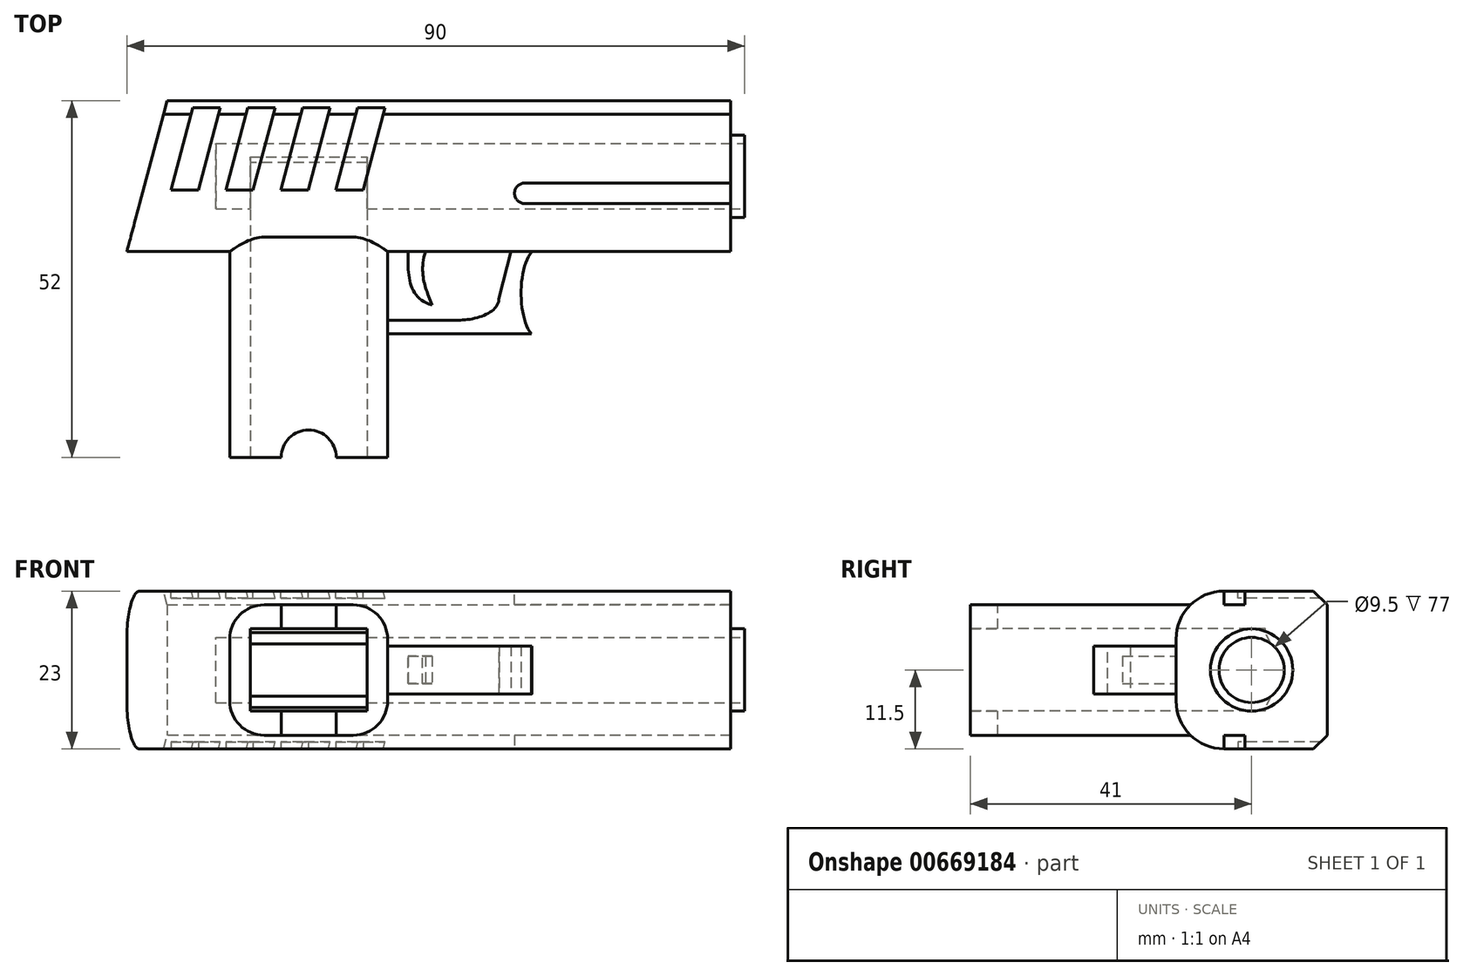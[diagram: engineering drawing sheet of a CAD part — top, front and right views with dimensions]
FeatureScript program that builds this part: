
annotation { "Feature Type Name" : "Feature", "Feature Type Description" : "" }
export const myFeature = defineFeature(function(context is Context, id is Id, definition is map)
    precondition{}
    {
        {
            var Q0;
            Q0=qCreatedBy(makeId("Top.planeOp"),FACE);
            var sketch = newSketch(context, id + "F0", { "sketchPlane" : qUnion([Q0])});
            skLineSegment(sketch, "E0", {"start": v(49.59, 22) * mm, "end": v(49.59, 0) * mm});
            skLineSegment(sketch, "E1", {"start": v(49.59, 0) * mm, "end": v(-0.41, 0) * mm});
            skLineSegment(sketch, "E2", {"start": v(-0.41, 0) * mm, "end": v(-0.41, -30) * mm});
            skLineSegment(sketch, "E3", {"start": v(-0.41, -30) * mm, "end": v(-23.41, -30) * mm});
            skLineSegment(sketch, "E4", {"start": v(-23.41, -30) * mm, "end": v(-23.41, 0) * mm});
            skLineSegment(sketch, "E5", {"start": v(-23.41, 0) * mm, "end": v(-38.41, 0) * mm});
            skLineSegment(sketch, "E6", {"start": v(-32.52, 22) * mm, "end": v(49.59, 22) * mm});
            skLineSegment(sketch, "E7", {"start": v(-38.41, 0) * mm, "end": v(-32.52, 22) * mm});
            skSolve(sketch);
        }
        {
            var Q0;
            Q0=makeQuery(id+"F0.imprint","IMPRINT",FACE,{"disambiguationData":[TD([[makeQuery(id+"F0.imprint","IMPRINT",EDGE,{"derivedFrom":sQuery(id+"F0.wireOp",EDGE,"E0")}),-1.0]])]});
            extrude(context, id + "F1", {"entities" : qUnion([Q0]), "endBound" : BoundingType.SYMMETRIC, "depth" : 19 * mm, "offsetDistance" : 25 * mm});
        }
        {
            var Q0;
            Q0=makeQuery(id+"F1.opExtrude","CAP_FACE",FACE,{"disambiguationData":[OSD([sQuery(id+"F0.wireOp",EDGE,"E0"),sQuery(id+"F0.wireOp",EDGE,"E1"),sQuery(id+"F0.wireOp",EDGE,"E2"),sQuery(id+"F0.wireOp",EDGE,"E3"),sQuery(id+"F0.wireOp",EDGE,"E4"),sQuery(id+"F0.wireOp",EDGE,"E5"),sQuery(id+"F0.wireOp",EDGE,"NrAtbqXy-u60X-30Q2-Hl1u-7mO5fDowlZYq"),sQuery(id+"F0.wireOp",EDGE,"E6")])],"isStart":false});
            var sketch = newSketch(context, id + "F2", { "sketchPlane" : qUnion([Q0])});
            skLineSegment(sketch, "E8", {"start": v(-32.52, 22) * mm, "end": v(49.59, 22) * mm});
            skLineSegment(sketch, "E9", {"start": v(49.59, 22) * mm, "end": v(49.59, 0) * mm});
            skLineSegment(sketch, "E10", {"start": v(49.59, 0) * mm, "end": v(-38.41, 0) * mm});
            skLineSegment(sketch, "E11", {"start": v(-38.41, 0) * mm, "end": v(-32.52, 22) * mm});
            skSolve(sketch);
        }
        {
            var Q0;
            Q0=makeQuery(id+"F2.imprint","IMPRINT",FACE,{"disambiguationData":[TD([[makeQuery(id+"F2.imprint","IMPRINT",EDGE,{"derivedFrom":sQuery(id+"F2.wireOp",EDGE,"E8")}),-1.0]])]});
            extrude(context, id + "F3", {"entities" : qUnion([Q0]), "operationType" : NewBodyOperationType.ADD, "depth" : 2 * mm, "offsetDistance" : 25 * mm});
        }
        {
            var Q0;
            Q0=makeQuery(id+"F1.opExtrude","CAP_FACE",FACE,{"disambiguationData":[OSD([sQuery(id+"F0.wireOp",EDGE,"E0"),sQuery(id+"F0.wireOp",EDGE,"E1"),sQuery(id+"F0.wireOp",EDGE,"E2"),sQuery(id+"F0.wireOp",EDGE,"E3"),sQuery(id+"F0.wireOp",EDGE,"E4"),sQuery(id+"F0.wireOp",EDGE,"E5"),sQuery(id+"F0.wireOp",EDGE,"E6"),sQuery(id+"F0.wireOp",EDGE,"E7")])],"isStart":true});
            var sketch = newSketch(context, id + "F4", { "sketchPlane" : qUnion([Q0])});
            skLineSegment(sketch, "E12", {"start": v(-38.41, 0) * mm, "end": v(49.59, 0) * mm});
            skLineSegment(sketch, "E13", {"start": v(49.59, 0) * mm, "end": v(49.59, -22) * mm});
            skLineSegment(sketch, "E14", {"start": v(49.59, -22) * mm, "end": v(-32.52, -22) * mm});
            skLineSegment(sketch, "E15", {"start": v(-38.41, 0) * mm, "end": v(-32.52, -22) * mm});
            skSolve(sketch);
        }
        {
            var Q0;
            {var subQ0=sQuery(id+"F4.wireOp",EDGE,"E13");Q0=makeQuery(id+"F4.imprint","IMPRINT",FACE,{"disambiguationData":[TD([[makeQuery(id+"F4.imprint","IMPRINT",EDGE,{"derivedFrom":subQ0}),1.0]])]});}
            extrude(context, id + "F5", {"entities" : qUnion([Q0]), "operationType" : NewBodyOperationType.ADD, "depth" : 2 * mm, "offsetDistance" : 25 * mm});
        }
        {
            var Q0;
            Q0=makeQuery(id+"F1.opExtrude","SWEPT_FACE",FACE,{"disambiguationData":[OSD([sQuery(id+"F0.wireOp",EDGE,"E3")])]});
            var sketch = newSketch(context, id + "F6", { "sketchPlane" : qUnion([Q0])});
            skLineSegment(sketch, "E16.bottom", {"start": v(-20.41, -6) * mm, "end": v(-3.41, -6) * mm});
            skLineSegment(sketch, "E16.top", {"start": v(-20.41, 6) * mm, "end": v(-3.41, 6) * mm});
            skLineSegment(sketch, "E16.left", {"start": v(-20.41, -6) * mm, "end": v(-20.41, 6) * mm});
            skLineSegment(sketch, "E16.right", {"start": v(-3.41, -6) * mm, "end": v(-3.41, 6) * mm});
            skSolve(sketch);
        }
        {
            var Q0;
            Q0=makeQuery(id+"F6.imprint","IMPRINT",FACE,{"disambiguationData":[TD([[makeQuery(id+"F6.imprint","IMPRINT",EDGE,{"derivedFrom":sQuery(id+"F6.wireOp",EDGE,"E16.bottom")}),1.0]])]});
            extrude(context, id + "F7", {"entities" : qUnion([Q0]), "operationType" : NewBodyOperationType.REMOVE, "oppositeDirection" : true, "depth" : 43 * mm, "offsetDistance" : 25 * mm});
        }
        {
            var Q0;
            Q0=makeQuery(id+"FhM5kjjk5gzZKvL_1.boolean.opBoolean","MERGE",FACE,{"derivedFrom":[makeQuery(id+"FprcvruxTVWMNmV_1.boolean.opBoolean","MERGE",FACE,{"derivedFrom":[makeQuery(id+"F1.opExtrude","SWEPT_FACE",FACE,{"disambiguationData":[OSD([sQuery(id+"F0.wireOp",EDGE,"E0")])]}),makeQuery(id+"FprcvruxTVWMNmV_1.opExtrude","SWEPT_FACE",FACE,{"disambiguationData":[OSD([sQuery(id+"F2.wireOp",EDGE,"sqEqtX76-uPf1-DTDx-mvrF-cFKsv4BRStOY")])]})]}),makeQuery(id+"FhM5kjjk5gzZKvL_1.opExtrude","SWEPT_FACE",FACE,{"disambiguationData":[OSD([sQuery(id+"FZzf1d15XStZTvC_1.wireOp",EDGE,"yVIWi02G-LVN5-e66G-xl55-ItvdXD6Bzk6r")])]})]});
            var sketch = newSketch(context, id + "F8", { "sketchPlane" : qUnion([Q0])});
            skCircle(sketch, "E17", {"center": v(11, 0) * mm, "radius": 4.75 * mm});
            skSolve(sketch);
        }
        {
            var Q0;
            Q0=makeQuery(id+"F8.imprint","IMPRINT",FACE,{"disambiguationData":[TD([[makeQuery(id+"F8.imprint","IMPRINT",EDGE,{"derivedFrom":sQuery(id+"F8.wireOp",EDGE,"E17")}),1.0]])]});
            extrude(context, id + "F9", {"entities" : qUnion([Q0]), "operationType" : NewBodyOperationType.REMOVE, "oppositeDirection" : true, "depth" : 75 * mm, "offsetDistance" : 25 * mm});
        }
        {
            var Q0;
            Q0=makeQuery(id+"F1.opExtrude","CAP_FACE",FACE,{"disambiguationData":[OSD([sQuery(id+"F0.wireOp",EDGE,"E0"),sQuery(id+"F0.wireOp",EDGE,"E1"),sQuery(id+"F0.wireOp",EDGE,"E2"),sQuery(id+"F0.wireOp",EDGE,"E3"),sQuery(id+"F0.wireOp",EDGE,"E4"),sQuery(id+"F0.wireOp",EDGE,"E5"),sQuery(id+"F0.wireOp",EDGE,"E6"),sQuery(id+"F0.wireOp",EDGE,"E7")])],"isStart":false});
            var sketch = newSketch(context, id + "F10", { "sketchPlane" : qUnion([Q0])});
            skCircle(sketch, "E18", {"center": v(-11.91, -30) * mm, "radius": 4 * mm});
            skSolve(sketch);
        }
        {
            var Q0;
            {var subQ0=sQuery(id+"F10.wireOp",EDGE,"E18");var subQ1=makeQuery(id+"F1.opExtrude","CAP_EDGE",EDGE,{"disambiguationData":[OSD([sQuery(id+"F0.wireOp",EDGE,"E3")])],"isStart":false});var subQ2=makeQuery(id+"F10.imprint","INTERSECT",VERTEX,{"disambiguationData":[OD(0.0)],"derivedFrom":[subQ1,subQ0]});Q0=makeQuery(id+"F10.imprint","IMPRINT",FACE,{"disambiguationData":[TD([[makeQuery(id+"F10.imprint","IMPRINT",EDGE,{"disambiguationData":[TD([[subQ2,-1.0]])],"derivedFrom":subQ0}),1.0]])]});}
            extrude(context, id + "F11", {"entities" : qUnion([Q0]), "operationType" : NewBodyOperationType.REMOVE, "oppositeDirection" : true, "depth" : 25 * mm, "offsetDistance" : 25 * mm});
        }
        {
            var Q0;
            Q0=makeQuery(id+"F5.boolean.opBoolean","MERGE",FACE,{"derivedFrom":[makeQuery(id+"F3.boolean.opBoolean","MERGE",FACE,{"derivedFrom":[makeQuery(id+"F1.opExtrude","SWEPT_FACE",FACE,{"disambiguationData":[OSD([sQuery(id+"F0.wireOp",EDGE,"E0")])]}),makeQuery(id+"F3.opExtrude","SWEPT_FACE",FACE,{"disambiguationData":[OSD([sQuery(id+"F2.wireOp",EDGE,"E9")])]})]}),makeQuery(id+"F5.opExtrude","SWEPT_FACE",FACE,{"disambiguationData":[OSD([sQuery(id+"F4.wireOp",EDGE,"E13")])]})]});
            var sketch = newSketch(context, id + "F12", { "sketchPlane" : qUnion([Q0])});
            skCircle(sketch, "E19", {"center": v(11, 0) * mm, "radius": 4.75 * mm});
            skCircle(sketch, "E20", {"center": v(11, 0) * mm, "radius": 6 * mm});
            skSolve(sketch);
        }
        {
            var Q0;
            Q0=makeQuery(id+"F12.imprint","IMPRINT",FACE,{"disambiguationData":[TD([[makeQuery(id+"F12.imprint","IMPRINT",EDGE,{"derivedFrom":sQuery(id+"F12.wireOp",EDGE,"E19")}),-1.0]])]});
            extrude(context, id + "F13", {"entities" : qUnion([Q0]), "operationType" : NewBodyOperationType.ADD, "depth" : 2 * mm, "offsetDistance" : 25 * mm});
        }
        {
            var Q0;
            Q0=makeQuery(id+"F9.boolean.opBoolean","INTERSECT",EDGE,{"disambiguationData":[OD(0.0)],"derivedFrom":[makeQuery(id+"F7.boolean.opBoolean","COPY",FACE,{"derivedFrom":makeQuery(id+"F7.opExtrude","CAP_FACE",FACE,{"disambiguationData":[OSD([sQuery(id+"F6.wireOp",EDGE,"E16.bottom"),sQuery(id+"F6.wireOp",EDGE,"E16.top"),sQuery(id+"F6.wireOp",EDGE,"E16.left"),sQuery(id+"F6.wireOp",EDGE,"E16.right")])],"isStart":false})}),makeQuery(id+"F9.opExtrude","SWEPT_FACE",FACE,{"disambiguationData":[OSD([sQuery(id+"F8.wireOp",EDGE,"E17")])]})]});
            chamfer(context, id + "F14", {"entities" : qUnion([Q0]), "width" : 2 * mm, "tangentPropagation" : true});
        }
        {
            var Q0;
            Q0=makeQuery(id+"F9.boolean.opBoolean","INTERSECT",EDGE,{"disambiguationData":[OD(1.0)],"derivedFrom":[makeQuery(id+"F7.boolean.opBoolean","COPY",FACE,{"derivedFrom":makeQuery(id+"F7.opExtrude","CAP_FACE",FACE,{"disambiguationData":[OSD([sQuery(id+"F6.wireOp",EDGE,"E16.bottom"),sQuery(id+"F6.wireOp",EDGE,"E16.top"),sQuery(id+"F6.wireOp",EDGE,"E16.left"),sQuery(id+"F6.wireOp",EDGE,"E16.right")])],"isStart":false})}),makeQuery(id+"F9.opExtrude","SWEPT_FACE",FACE,{"disambiguationData":[OSD([sQuery(id+"F8.wireOp",EDGE,"E17")])]})]});
            chamfer(context, id + "F15", {"entities" : qUnion([Q0]), "width" : 2 * mm, "tangentPropagation" : true});
        }
        {
            var Q0;
            Q0=makeQuery(id+"F5.opExtrude","CAP_EDGE",EDGE,{"disambiguationData":[OSD([sQuery(id+"F4.wireOp",EDGE,"E12")])],"isStart":false});
            fillet(context, id + "F16", {"entities" : qUnion([Q0]), "radius" : 7 * mm, "tangentPropagation" : true, "allowEdgeOverflow" : false});
        }
        {
            var Q0;
            Q0=makeQuery(id+"F3.opExtrude","CAP_EDGE",EDGE,{"disambiguationData":[OSD([sQuery(id+"F2.wireOp",EDGE,"E10")])],"isStart":false});
            fillet(context, id + "F17", {"entities" : qUnion([Q0]), "radius" : 7 * mm, "tangentPropagation" : true, "allowEdgeOverflow" : false});
        }
        {
            var Q0;
            Q0=makeQuery(id+"F5.opExtrude","CAP_FACE",FACE,{"disambiguationData":[OSD([sQuery(id+"F4.wireOp",EDGE,"E12"),sQuery(id+"F4.wireOp",EDGE,"E13"),sQuery(id+"F4.wireOp",EDGE,"E14"),sQuery(id+"F4.wireOp",EDGE,"E15")])],"isStart":false});
            var sketch = newSketch(context, id + "F18", { "sketchPlane" : qUnion([Q0])});
            skLineSegment(sketch, "E21", {"start": v(-28.52, -22) * mm, "end": v(-32, -9) * mm});
            skLineSegment(sketch, "E22", {"start": v(-32, -9) * mm, "end": v(-28, -9) * mm});
            skLineSegment(sketch, "E23", {"start": v(-28, -9) * mm, "end": v(-24.52, -22) * mm});
            skLineSegment(sketch, "E24", {"start": v(-20.52, -22) * mm, "end": v(-24, -9) * mm});
            skLineSegment(sketch, "E25", {"start": v(-24, -9) * mm, "end": v(-20, -9) * mm});
            skLineSegment(sketch, "E26", {"start": v(-20, -9) * mm, "end": v(-16.52, -22) * mm});
            skLineSegment(sketch, "E27", {"start": v(-12.52, -22) * mm, "end": v(-16, -9) * mm});
            skLineSegment(sketch, "E28", {"start": v(-16, -9) * mm, "end": v(-12, -9) * mm});
            skLineSegment(sketch, "E29", {"start": v(-12, -9) * mm, "end": v(-8.52, -22) * mm});
            skLineSegment(sketch, "E30", {"start": v(-4.52, -22) * mm, "end": v(-8, -9) * mm});
            skLineSegment(sketch, "E31", {"start": v(-8, -9) * mm, "end": v(-4, -9) * mm});
            skLineSegment(sketch, "E32", {"start": v(-4, -9) * mm, "end": v(-0.52, -22) * mm});
            skLineSegment(sketch, "E33.bottom", {"start": v(49.59, -7) * mm, "end": v(19.59, -7) * mm});
            skLineSegment(sketch, "E33.top", {"start": v(49.59, -10) * mm, "end": v(19.59, -10) * mm});
            skLineSegment(sketch, "E33.left", {"start": v(49.59, -7) * mm, "end": v(49.59, -10) * mm});
            skLineSegment(sketch, "E33.right", {"start": v(19.59, -7) * mm, "end": v(19.59, -10) * mm});
            skCircle(sketch, "E34", {"center": v(19.59, -8.5) * mm, "radius": 1.5 * mm});
            skSolve(sketch);
        }
        {
            var Q0;
            {var subQ0=sQuery(id+"F18.wireOp",EDGE,"E30");Q0=makeQuery(id+"F18.imprint","IMPRINT",FACE,{"disambiguationData":[TD([[makeQuery(id+"F18.imprint","IMPRINT",EDGE,{"derivedFrom":subQ0}),-1.0]])]});}
            var Q1;
            {var subQ0=sQuery(id+"F18.wireOp",EDGE,"E27");Q1=makeQuery(id+"F18.imprint","IMPRINT",FACE,{"disambiguationData":[TD([[makeQuery(id+"F18.imprint","IMPRINT",EDGE,{"derivedFrom":subQ0}),-1.0]])]});}
            var Q2;
            {var subQ0=sQuery(id+"F18.wireOp",EDGE,"E24");Q2=makeQuery(id+"F18.imprint","IMPRINT",FACE,{"disambiguationData":[TD([[makeQuery(id+"F18.imprint","IMPRINT",EDGE,{"derivedFrom":subQ0}),-1.0]])]});}
            var Q3;
            {var subQ0=sQuery(id+"F18.wireOp",EDGE,"E21");Q3=makeQuery(id+"F18.imprint","IMPRINT",FACE,{"disambiguationData":[TD([[makeQuery(id+"F18.imprint","IMPRINT",EDGE,{"derivedFrom":subQ0}),-1.0]])]});}
            extrude(context, id + "F19", {"entities" : qUnion([Q0, Q1, Q2, Q3]), "operationType" : NewBodyOperationType.REMOVE, "oppositeDirection" : true, "depth" : 1 * mm, "offsetDistance" : 25 * mm});
        }
        {
            var Q0;
            {var subQ0=sQuery(id+"F18.wireOp",EDGE,"E33.bottom");Q0=makeQuery(id+"F18.imprint","IMPRINT",FACE,{"disambiguationData":[TD([[makeQuery(id+"F18.imprint","IMPRINT",EDGE,{"derivedFrom":subQ0}),1.0]])]});}
            var Q1;
            {var subQ0=sQuery(id+"F18.wireOp",EDGE,"E33.right");Q1=makeQuery(id+"F18.imprint","IMPRINT",FACE,{"disambiguationData":[TD([[makeQuery(id+"F18.imprint","IMPRINT",EDGE,{"derivedFrom":subQ0}),-1.0]])]});}
            var Q2;
            {var subQ0=sQuery(id+"F18.wireOp",EDGE,"E33.right");Q2=makeQuery(id+"F18.imprint","IMPRINT",FACE,{"disambiguationData":[TD([[makeQuery(id+"F18.imprint","IMPRINT",EDGE,{"derivedFrom":subQ0}),1.0]])]});}
            extrude(context, id + "F20", {"entities" : qUnion([Q0, Q1, Q2]), "operationType" : NewBodyOperationType.REMOVE, "oppositeDirection" : true, "depth" : 2 * mm, "offsetDistance" : 25 * mm});
        }
        {
            var Q0;
            Q0=makeQuery(id+"F3.opExtrude","CAP_FACE",FACE,{"disambiguationData":[OSD([sQuery(id+"F2.wireOp",EDGE,"E8"),sQuery(id+"F2.wireOp",EDGE,"E9"),sQuery(id+"F2.wireOp",EDGE,"E10"),sQuery(id+"F2.wireOp",EDGE,"E11")])],"isStart":false});
            var sketch = newSketch(context, id + "F21", { "sketchPlane" : qUnion([Q0])});
            skLineSegment(sketch, "E35", {"start": v(-32, 9) * mm, "end": v(-28, 9) * mm});
            skLineSegment(sketch, "E36", {"start": v(-28, 9) * mm, "end": v(-24.52, 22) * mm});
            skLineSegment(sketch, "E37", {"start": v(-20.52, 22) * mm, "end": v(-24, 9) * mm});
            skLineSegment(sketch, "E38", {"start": v(-24, 9) * mm, "end": v(-20, 9) * mm});
            skLineSegment(sketch, "E39", {"start": v(-20, 9) * mm, "end": v(-16.52, 22) * mm});
            skLineSegment(sketch, "E40", {"start": v(-12.52, 22) * mm, "end": v(-16, 9) * mm});
            skLineSegment(sketch, "E41", {"start": v(-16, 9) * mm, "end": v(-12, 9) * mm});
            skLineSegment(sketch, "E42", {"start": v(-12, 9) * mm, "end": v(-8.52, 22) * mm});
            skLineSegment(sketch, "E43", {"start": v(-4.52, 22) * mm, "end": v(-8, 9) * mm});
            skLineSegment(sketch, "E44", {"start": v(-8, 9) * mm, "end": v(-4, 9) * mm});
            skLineSegment(sketch, "E45", {"start": v(-4, 9) * mm, "end": v(-0.52, 22) * mm});
            skLineSegment(sketch, "E46", {"start": v(-28.52, 22) * mm, "end": v(-32, 9) * mm});
            skLineSegment(sketch, "E47.bottom", {"start": v(49.59, 7) * mm, "end": v(19.59, 7) * mm});
            skLineSegment(sketch, "E47.top", {"start": v(49.59, 10) * mm, "end": v(19.59, 10) * mm});
            skLineSegment(sketch, "E47.left", {"start": v(49.59, 7) * mm, "end": v(49.59, 10) * mm});
            skLineSegment(sketch, "E47.right", {"start": v(19.59, 7) * mm, "end": v(19.59, 10) * mm});
            skCircle(sketch, "E48", {"center": v(19.59, 8.5) * mm, "radius": 1.5 * mm});
            skSolve(sketch);
        }
        {
            var Q0;
            Q0=makeQuery(id+"F21.imprint","IMPRINT",FACE,{"disambiguationData":[TD([[makeQuery(id+"F21.imprint","IMPRINT",EDGE,{"derivedFrom":sQuery(id+"F21.wireOp",EDGE,"E35")}),1.0]])]});
            var Q1;
            {var subQ0=sQuery(id+"F21.wireOp",EDGE,"E37");Q1=makeQuery(id+"F21.imprint","IMPRINT",FACE,{"disambiguationData":[TD([[makeQuery(id+"F21.imprint","IMPRINT",EDGE,{"derivedFrom":subQ0}),1.0]])]});}
            var Q2;
            {var subQ0=sQuery(id+"F21.wireOp",EDGE,"E40");Q2=makeQuery(id+"F21.imprint","IMPRINT",FACE,{"disambiguationData":[TD([[makeQuery(id+"F21.imprint","IMPRINT",EDGE,{"derivedFrom":subQ0}),1.0]])]});}
            var Q3;
            {var subQ0=sQuery(id+"F21.wireOp",EDGE,"E43");Q3=makeQuery(id+"F21.imprint","IMPRINT",FACE,{"disambiguationData":[TD([[makeQuery(id+"F21.imprint","IMPRINT",EDGE,{"derivedFrom":subQ0}),1.0]])]});}
            extrude(context, id + "F22", {"entities" : qUnion([Q0, Q1, Q2, Q3]), "operationType" : NewBodyOperationType.REMOVE, "oppositeDirection" : true, "depth" : 1 * mm, "offsetDistance" : 25 * mm});
        }
        {
            var Q0;
            {var subQ0=sQuery(id+"F21.wireOp",EDGE,"E47.bottom");Q0=makeQuery(id+"F21.imprint","IMPRINT",FACE,{"disambiguationData":[TD([[makeQuery(id+"F21.imprint","IMPRINT",EDGE,{"derivedFrom":subQ0}),1.0]])]});}
            var Q1;
            {var subQ0=sQuery(id+"F21.wireOp",EDGE,"E47.right");Q1=makeQuery(id+"F21.imprint","IMPRINT",FACE,{"disambiguationData":[TD([[makeQuery(id+"F21.imprint","IMPRINT",EDGE,{"derivedFrom":subQ0}),-1.0]])]});}
            var Q2;
            {var subQ0=sQuery(id+"F21.wireOp",EDGE,"E47.right");Q2=makeQuery(id+"F21.imprint","IMPRINT",FACE,{"disambiguationData":[TD([[makeQuery(id+"F21.imprint","IMPRINT",EDGE,{"derivedFrom":subQ0}),1.0]])]});}
            extrude(context, id + "F23", {"entities" : qUnion([Q0, Q1, Q2]), "operationType" : NewBodyOperationType.REMOVE, "oppositeDirection" : true, "depth" : 2 * mm, "offsetDistance" : 25 * mm});
        }
        {
            var Q0;
            Q0=makeQuery(id+"F1.opExtrude","CAP_EDGE",EDGE,{"disambiguationData":[OSD([sQuery(id+"F0.wireOp",EDGE,"E2")])],"isStart":true});
            fillet(context, id + "F24", {"entities" : qUnion([Q0]), "radius" : 5 * mm, "tangentPropagation" : true, "allowEdgeOverflow" : false});
        }
        {
            var Q0;
            Q0=makeQuery(id+"F1.opExtrude","CAP_EDGE",EDGE,{"disambiguationData":[OSD([sQuery(id+"F0.wireOp",EDGE,"E4")])],"isStart":true});
            fillet(context, id + "F25", {"entities" : qUnion([Q0]), "radius" : 5 * mm, "tangentPropagation" : true, "allowEdgeOverflow" : false});
        }
        {
            var Q0;
            Q0=makeQuery(id+"F1.opExtrude","CAP_EDGE",EDGE,{"disambiguationData":[OSD([sQuery(id+"F0.wireOp",EDGE,"E4")])],"isStart":false});
            fillet(context, id + "F26", {"entities" : qUnion([Q0]), "radius" : 5 * mm, "tangentPropagation" : true, "allowEdgeOverflow" : false});
        }
        {
            var Q0;
            Q0=makeQuery(id+"F1.opExtrude","CAP_EDGE",EDGE,{"disambiguationData":[OSD([sQuery(id+"F0.wireOp",EDGE,"E2")])],"isStart":false});
            fillet(context, id + "F27", {"entities" : qUnion([Q0]), "radius" : 5 * mm, "tangentPropagation" : true, "allowEdgeOverflow" : false});
        }
        {
            var Q0;
            Q0=qCreatedBy(makeId("Top.planeOp"),FACE);
            var sketch = newSketch(context, id + "F28", { "sketchPlane" : qUnion([Q0])});
            skLineSegment(sketch, "E49", {"start": v(0, 0) * mm, "end": v(17.59, 0) * mm});
            skLineSegment(sketch, "E50", {"start": v(-0.41, 0) * mm, "end": v(0, 0) * mm});
            skLineSegment(sketch, "E51", {"start": v(-0.41, 0) * mm, "end": v(-2.17, -10) * mm});
            skLineSegment(sketch, "E52", {"start": v(17.59, 0) * mm, "end": v(20.59, 0) * mm});
            skLineSegment(sketch, "E53", {"start": v(-2.17, -10) * mm, "end": v(-2.53, -12) * mm});
            skLineSegment(sketch, "E54", {"start": v(-2.53, -12) * mm, "end": v(20.52, -12) * mm});
            skFitSpline(sketch, "E55", {"points": [v(20.52, -12) * mm, v(20.59, 0) * mm], "startDerivative": vector(-5.97, 7.28) * mm, "endDerivative": vector(6.17, 7.25) * mm});
            skLineSegment(sketch, "E56", {"start": v(18.53, -2.42) * mm, "end": v(18.53, -9.57) * mm, "construction": true});
            skLineSegment(sketch, "E57", {"start": v(-2.17, -10) * mm, "end": v(9.83, -10) * mm});
            skLineSegment(sketch, "E58", {"start": v(17.59, 0) * mm, "end": v(15.83, -6.67) * mm});
            skFitSpline(sketch, "E59", {"points": [v(9.83, -10) * mm, v(15.83, -6.67) * mm], "startDerivative": vector(7.71, 0) * mm, "endDerivative": vector(0, 7.16) * mm});
            skLineSegment(sketch, "E60", {"start": v(9.83, -10) * mm, "end": v(15.83, -10) * mm, "construction": true});
            skLineSegment(sketch, "E61", {"start": v(15.83, -6.67) * mm, "end": v(15.83, -10) * mm, "construction": true});
            skFitSpline(sketch, "E62", {"points": [v(5.09, 0) * mm, v(6.09, -7.8) * mm], "startDerivative": vector(-2.9, -9.95) * mm, "endDerivative": vector(3, -7.51) * mm});
            skFitSpline(sketch, "E63", {"points": [v(6.09, -7.8) * mm, v(2.59, 0) * mm], "startDerivative": vector(-10.7, 2.88) * mm, "endDerivative": vector(0.27, 10.1) * mm});
            skLineSegment(sketch, "E64", {"start": v(2.59, 0) * mm, "end": v(2.5, -8.86) * mm, "construction": true});
            skLineSegment(sketch, "E65", {"start": v(5.09, 0) * mm, "end": v(2.5, -8.86) * mm, "construction": true});
            skLineSegment(sketch, "E66", {"start": v(5.09, 0) * mm, "end": v(5.09, -8.9) * mm, "construction": true});
            skSolve(sketch);
        }
        {
            var Q0;
            Q0=makeQuery(id+"F28.imprint","IMPRINT",FACE,{"disambiguationData":[TD([[makeQuery(id+"F28.imprint","IMPRINT",EDGE,{"derivedFrom":sQuery(id+"F28.wireOp",EDGE,"E52")}),-1.0]])]});
            extrude(context, id + "F29", {"entities" : qUnion([Q0]), "operationType" : NewBodyOperationType.ADD, "endBound" : BoundingType.SYMMETRIC, "depth" : 7 * mm, "offsetDistance" : 25 * mm});
        }
        {
            var Q0;
            {var subQ0=sQuery(id+"F28.wireOp",EDGE,"E62");Q0=makeQuery(id+"F28.imprint","IMPRINT",FACE,{"disambiguationData":[TD([[makeQuery(id+"F28.imprint","IMPRINT",EDGE,{"derivedFrom":subQ0}),-1.0]])]});}
            extrude(context, id + "F30", {"entities" : qUnion([Q0]), "operationType" : NewBodyOperationType.ADD, "endBound" : BoundingType.SYMMETRIC, "depth" : 4 * mm, "offsetDistance" : 25 * mm});
        }
        {
            var Q0;
            {var subQ0=sQuery(id+"F2.wireOp",EDGE,"E8");Q0=makeQuery(id+"F22.boolean.opBoolean","SPLIT",EDGE,{"disambiguationData":[TD([makeQuery(id+"F1.opExtrude","SWEPT_FACE",FACE,{"disambiguationData":[OSD([sQuery(id+"F0.wireOp",EDGE,"E0")])]})])],"derivedFrom":makeQuery(id+"F3.opExtrude","CAP_EDGE",EDGE,{"disambiguationData":[OSD([subQ0])],"isStart":false})});}
            chamfer(context, id + "F31", {"entities" : qUnion([Q0]), "width" : 2 * mm, "tangentPropagation" : true});
        }
        {
            var Q0;
            {var subQ0=sQuery(id+"F4.wireOp",EDGE,"E14");Q0=makeQuery(id+"F19.boolean.opBoolean","SPLIT",EDGE,{"disambiguationData":[TD([makeQuery(id+"F1.opExtrude","SWEPT_FACE",FACE,{"disambiguationData":[OSD([sQuery(id+"F0.wireOp",EDGE,"E0")])]})])],"derivedFrom":makeQuery(id+"F5.opExtrude","CAP_EDGE",EDGE,{"disambiguationData":[OSD([subQ0])],"isStart":false})});}
            chamfer(context, id + "F32", {"entities" : qUnion([Q0]), "width" : 2 * mm, "tangentPropagation" : true});
        }
    });
